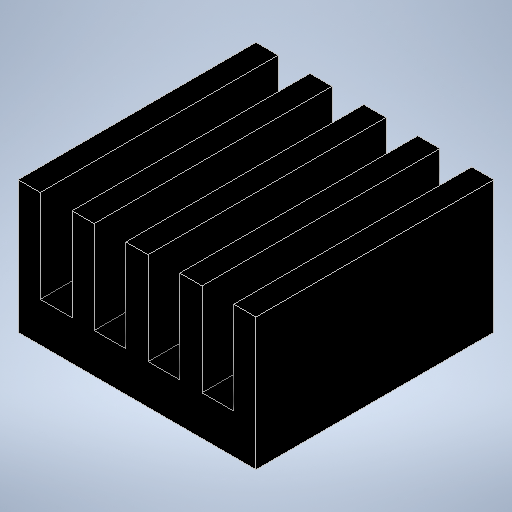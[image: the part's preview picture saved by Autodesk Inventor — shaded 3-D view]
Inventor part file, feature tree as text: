
AUTODESK INVENTOR PART (.ipt)
format: ipt  version: 2025 (Build 290162000, 162)  size: 198,144 bytes
history: native  units: mm
features: extrude x1, sketch x1
ambient origin geometry x8: Origin, YZ Plane, XZ Plane, XY Plane, X Axis, Y Axis, Z Axis, Center Point
bodies: Solid1 (feature_tree)
feature tree (2):
  extrude  "Extrusion1"  Depth=5.0mm
  sketch  "Sketch1"  dims[d0=9.0mm d2=5.0mm d3=1.2mm d4=3.5mm d5=9.0mm d6=0.0mm]
